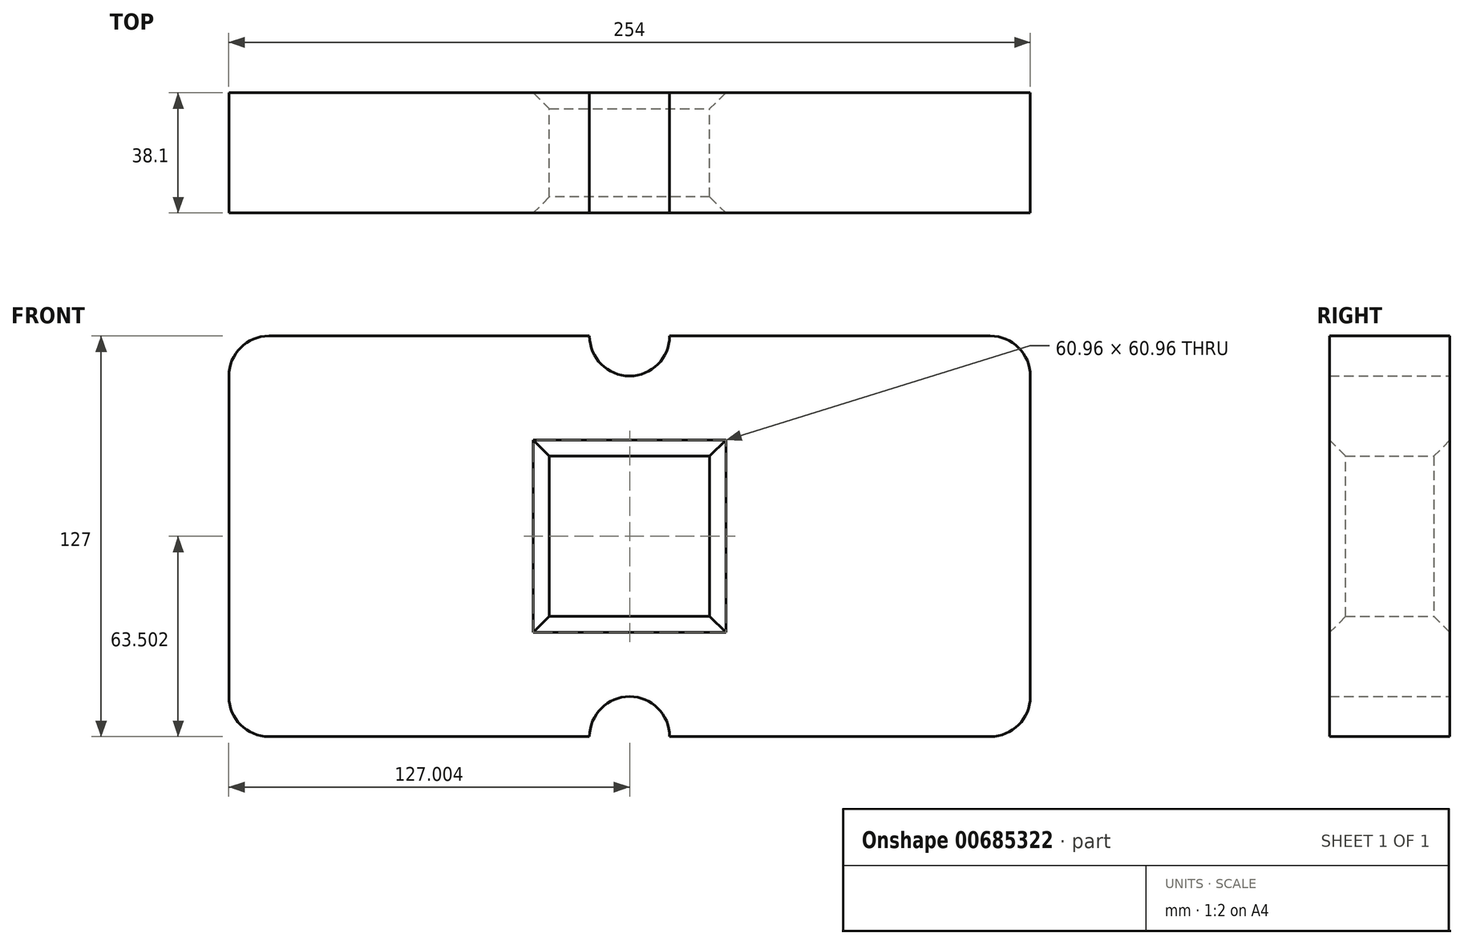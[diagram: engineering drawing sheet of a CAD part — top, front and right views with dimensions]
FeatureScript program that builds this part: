
annotation { "Feature Type Name" : "Feature", "Feature Type Description" : "" }
export const myFeature = defineFeature(function(context is Context, id is Id, definition is map)
    precondition{}
    {
        {
            var Q0;
            Q0=qCreatedBy(makeId("Front.planeOp"),FACE);
            var sketch = newSketch(context, id + "F0", { "sketchPlane" : qUnion([Q0])});
            skLineSegment(sketch, "E0.bottom", {"start": v(-121.39, -52.4) * mm, "end": v(-19.79, -52.4) * mm});
            skLineSegment(sketch, "E0.top", {"start": v(-121.39, 74.6) * mm, "end": v(-19.79, 74.6) * mm});
            skLineSegment(sketch, "E0.left", {"start": v(-134.09, -39.7) * mm, "end": v(-134.09, 61.9) * mm});
            skLineSegment(sketch, "E0.right", {"start": v(119.91, -39.7) * mm, "end": v(119.91, 61.9) * mm});
            skPoint(sketch, "E1.visualSharp", {"position": v(-134.09, 74.6) * mm});
            skArc(sketch, "E1.filletArc", {"start": v(-121.39, 74.6) * mm, "mid": v(-130.37, 70.87) * mm, "end": v(-134.09, 61.9) * mm});
            skPoint(sketch, "E2.visualSharp", {"position": v(119.91, 74.6) * mm});
            skArc(sketch, "E2.filletArc", {"start": v(119.91, 61.9) * mm, "mid": v(116.2, 70.87) * mm, "end": v(107.21, 74.6) * mm});
            skPoint(sketch, "E3.visualSharp", {"position": v(119.91, -52.4) * mm});
            skArc(sketch, "E3.filletArc", {"start": v(107.21, -52.4) * mm, "mid": v(116.2, -48.69) * mm, "end": v(119.91, -39.7) * mm});
            skPoint(sketch, "E4.visualSharp", {"position": v(-134.09, -52.4) * mm});
            skArc(sketch, "E4.filletArc", {"start": v(-134.09, -39.7) * mm, "mid": v(-130.37, -48.69) * mm, "end": v(-121.39, -52.4) * mm});
            skArc(sketch, "E5", {"start": v(-19.79, 74.6) * mm, "mid": v(-7.09, 61.9) * mm, "end": v(5.61, 74.6) * mm});
            skArc(sketch, "E6", {"start": v(5.61, -52.4) * mm, "mid": v(-7.09, -39.7) * mm, "end": v(-19.79, -52.4) * mm});
            skLineSegment(sketch, "E7.trimOffspring", {"start": v(5.61, 74.6) * mm, "end": v(107.21, 74.6) * mm});
            skLineSegment(sketch, "E8.trimOffspring", {"start": v(5.61, -52.4) * mm, "end": v(107.21, -52.4) * mm});
            skLineSegment(sketch, "E9", {"start": v(18.31, 36.5) * mm, "end": v(18.31, -14.3) * mm});
            skLineSegment(sketch, "E10", {"start": v(18.31, -14.3) * mm, "end": v(-32.49, -14.3) * mm});
            skLineSegment(sketch, "E11", {"start": v(-32.49, -14.3) * mm, "end": v(-32.49, 36.5) * mm});
            skLineSegment(sketch, "E12", {"start": v(-32.49, 36.5) * mm, "end": v(18.31, 36.5) * mm});
            skSolve(sketch);
        }
        {
            var Q0;
            Q0=makeQuery(id+"F0.imprint","IMPRINT",FACE,{"disambiguationData":[TD([[makeQuery(id+"F0.imprint","IMPRINT",EDGE,{"derivedFrom":sQuery(id+"F0.wireOp",EDGE,"E0.bottom")}),1.0]])]});
            extrude(context, id + "F1", {"entities" : qUnion([Q0]), "depth" : 38.1 * mm, "offsetDistance" : 25.4 * mm});
        }
        {
            var Q0;
            Q0=makeQuery(id+"F1.opExtrude","CAP_EDGE",EDGE,{"disambiguationData":[OSD([sQuery(id+"F0.wireOp",EDGE,"E9")])],"isStart":false});
            var Q1;
            Q1=makeQuery(id+"F1.opExtrude","CAP_EDGE",EDGE,{"disambiguationData":[OSD([sQuery(id+"F0.wireOp",EDGE,"E10")])],"isStart":false});
            var Q2;
            Q2=makeQuery(id+"F1.opExtrude","CAP_EDGE",EDGE,{"disambiguationData":[OSD([sQuery(id+"F0.wireOp",EDGE,"E11")])],"isStart":false});
            var Q3;
            Q3=makeQuery(id+"F1.opExtrude","CAP_EDGE",EDGE,{"disambiguationData":[OSD([sQuery(id+"F0.wireOp",EDGE,"E12")])],"isStart":false});
            var Q4;
            Q4=makeQuery(id+"F1.opExtrude","CAP_EDGE",EDGE,{"disambiguationData":[OSD([sQuery(id+"F0.wireOp",EDGE,"E10")])],"isStart":true});
            var Q5;
            Q5=makeQuery(id+"F1.opExtrude","CAP_EDGE",EDGE,{"disambiguationData":[OSD([sQuery(id+"F0.wireOp",EDGE,"E11")])],"isStart":true});
            var Q6;
            Q6=makeQuery(id+"F1.opExtrude","CAP_EDGE",EDGE,{"disambiguationData":[OSD([sQuery(id+"F0.wireOp",EDGE,"E9")])],"isStart":true});
            var Q7;
            Q7=makeQuery(id+"F1.opExtrude","CAP_EDGE",EDGE,{"disambiguationData":[OSD([sQuery(id+"F0.wireOp",EDGE,"E12")])],"isStart":true});
            chamfer(context, id + "F2", {"entities" : qUnion([Q0, Q1, Q2, Q3, Q4, Q5, Q6, Q7]), "width" : 5.08 * mm, "tangentPropagation" : true});
        }
    });
